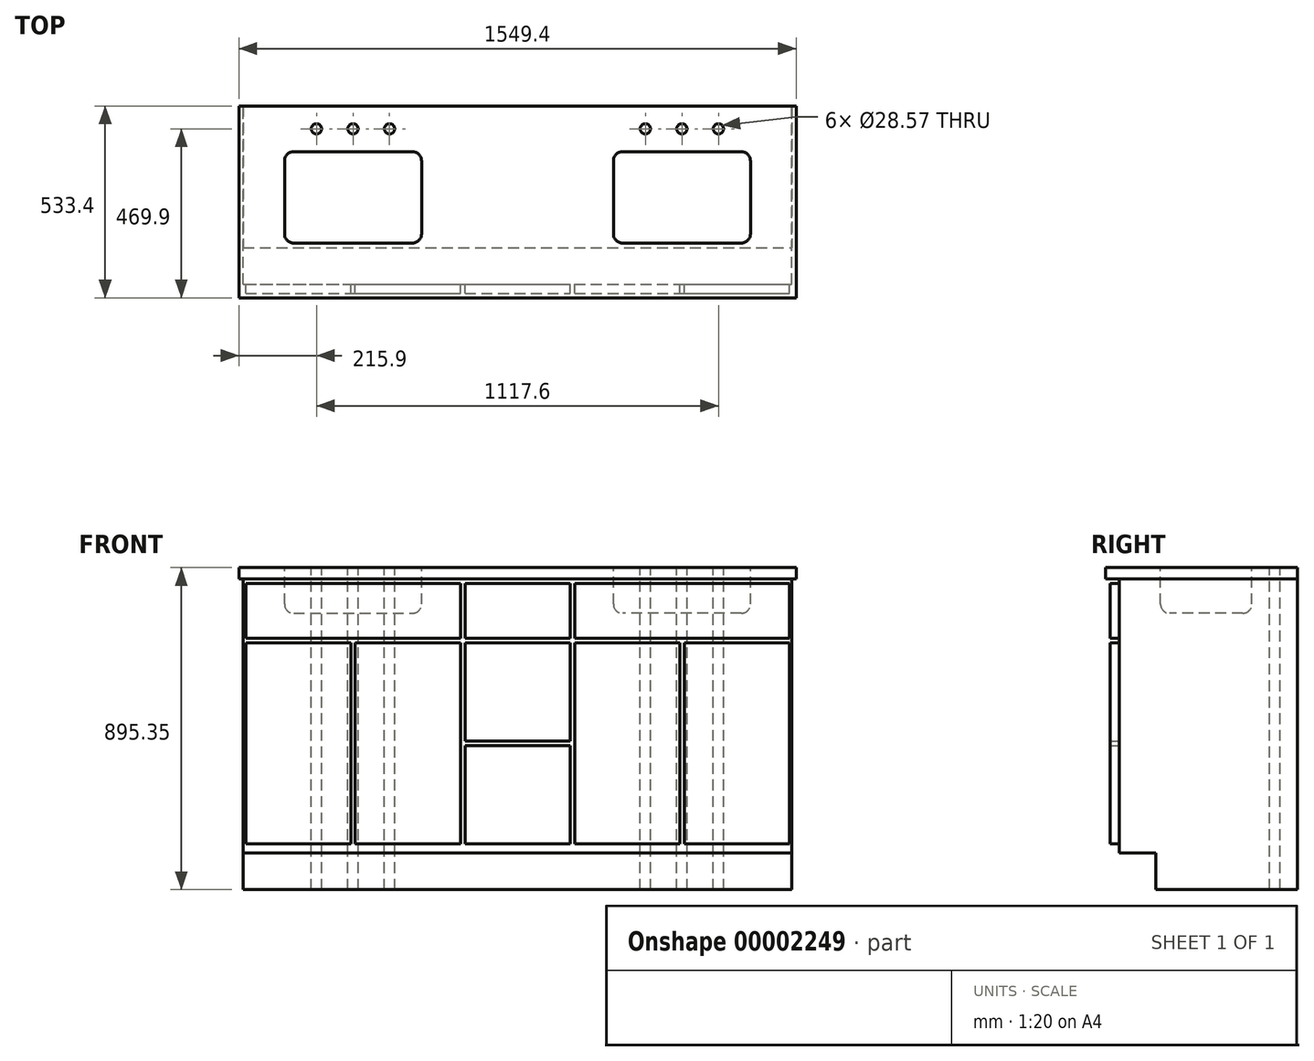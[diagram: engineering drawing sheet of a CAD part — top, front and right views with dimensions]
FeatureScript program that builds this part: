
annotation { "Feature Type Name" : "Feature", "Feature Type Description" : "" }
export const myFeature = defineFeature(function(context is Context, id is Id, definition is map)
    precondition{}
    {
        {
            var Q0;
            Q0=qCreatedBy(makeId("Right.planeOp"),FACE);
            var sketch = newSketch(context, id + "F0", { "sketchPlane" : qUnion([Q0])});
            skLineSegment(sketch, "E0.bottom", {"start": v(0, 0) * mm, "end": v(-393.7, 0) * mm});
            skLineSegment(sketch, "E0.left", {"start": v(0, 0) * mm, "end": v(0, 895.35) * mm});
            skLineSegment(sketch, "E0.right", {"start": v(-495.3, 101.6) * mm, "end": v(-495.3, 863.6) * mm});
            skLineSegment(sketch, "E1.top", {"start": v(-495.3, 101.6) * mm, "end": v(-393.7, 101.6) * mm});
            skLineSegment(sketch, "E1.right", {"start": v(-393.7, 0) * mm, "end": v(-393.7, 101.6) * mm});
            skLineSegment(sketch, "E2.bottom", {"start": v(-495.3, 863.6) * mm, "end": v(-533.4, 863.6) * mm});
            skLineSegment(sketch, "E2.top", {"start": v(0, 895.35) * mm, "end": v(-533.4, 895.35) * mm});
            skLineSegment(sketch, "E2.right", {"start": v(-533.4, 863.6) * mm, "end": v(-533.4, 895.35) * mm});
            skSolve(sketch);
        }
        {
            var Q0;
            Q0=makeQuery(id+"F0.imprint","IMPRINT",FACE,{"disambiguationData":[TD([[makeQuery(id+"F0.imprint","IMPRINT",EDGE,{"derivedFrom":sQuery(id+"F0.wireOp",EDGE,"E0.bottom")}),-1.0]])]});
            extrude(context, id + "F1", {"entities" : qUnion([Q0]), "oppositeDirection" : true, "depth" : 1524 * mm});
        }
        {
            var Q0;
            Q0=makeQuery(id+"F1.opExtrude","SWEPT_FACE",FACE,{"disambiguationData":[OSD([sQuery(id+"F0.wireOp",EDGE,"E0.right")])]});
            var sketch = newSketch(context, id + "F2", { "sketchPlane" : qUnion([Q0])});
            skLineSegment(sketch, "E3.bottom", {"start": v(-1517.65, 850.9) * mm, "end": v(-920.75, 850.9) * mm});
            skLineSegment(sketch, "E3.top", {"start": v(-1517.65, 698.5) * mm, "end": v(-920.75, 698.5) * mm});
            skLineSegment(sketch, "E3.left", {"start": v(-1517.65, 850.9) * mm, "end": v(-1517.65, 698.5) * mm});
            skLineSegment(sketch, "E3.right", {"start": v(-920.75, 850.9) * mm, "end": v(-920.75, 698.5) * mm});
            skLineSegment(sketch, "E4.bottom", {"start": v(-908.05, 850.9) * mm, "end": v(-615.95, 850.9) * mm});
            skLineSegment(sketch, "E4.top", {"start": v(-908.05, 698.5) * mm, "end": v(-615.95, 698.5) * mm});
            skLineSegment(sketch, "E4.left", {"start": v(-908.05, 850.9) * mm, "end": v(-908.05, 698.5) * mm});
            skLineSegment(sketch, "E4.right", {"start": v(-615.95, 850.9) * mm, "end": v(-615.95, 698.5) * mm});
            skLineSegment(sketch, "E5.bottom", {"start": v(-603.25, 850.9) * mm, "end": v(-6.35, 850.9) * mm});
            skLineSegment(sketch, "E5.top", {"start": v(-603.25, 698.5) * mm, "end": v(-6.35, 698.5) * mm});
            skLineSegment(sketch, "E5.left", {"start": v(-603.25, 850.9) * mm, "end": v(-603.25, 698.5) * mm});
            skLineSegment(sketch, "E5.right", {"start": v(-6.35, 850.9) * mm, "end": v(-6.35, 698.5) * mm});
            skLineSegment(sketch, "E6.bottom", {"start": v(-908.05, 685.8) * mm, "end": v(-615.95, 685.8) * mm});
            skLineSegment(sketch, "E6.top", {"start": v(-908.05, 412.75) * mm, "end": v(-615.95, 412.75) * mm});
            skLineSegment(sketch, "E6.left", {"start": v(-908.05, 685.8) * mm, "end": v(-908.05, 412.75) * mm});
            skLineSegment(sketch, "E6.right", {"start": v(-615.95, 685.8) * mm, "end": v(-615.95, 412.75) * mm});
            skLineSegment(sketch, "E7.bottom", {"start": v(-908.05, 400.05) * mm, "end": v(-615.95, 400.05) * mm});
            skLineSegment(sketch, "E7.top", {"start": v(-908.05, 127) * mm, "end": v(-615.95, 127) * mm});
            skLineSegment(sketch, "E7.left", {"start": v(-908.05, 400.05) * mm, "end": v(-908.05, 127) * mm});
            skLineSegment(sketch, "E7.right", {"start": v(-615.95, 400.05) * mm, "end": v(-615.95, 127) * mm});
            skLineSegment(sketch, "E8.bottom", {"start": v(-1517.65, 685.8) * mm, "end": v(-1225.55, 685.8) * mm});
            skLineSegment(sketch, "E8.top", {"start": v(-1517.65, 127) * mm, "end": v(-1225.55, 127) * mm});
            skLineSegment(sketch, "E8.left", {"start": v(-1517.65, 685.8) * mm, "end": v(-1517.65, 127) * mm});
            skLineSegment(sketch, "E8.right", {"start": v(-1225.55, 685.8) * mm, "end": v(-1225.55, 127) * mm});
            skLineSegment(sketch, "E9.bottom", {"start": v(-1212.85, 685.8) * mm, "end": v(-920.75, 685.8) * mm});
            skLineSegment(sketch, "E9.top", {"start": v(-1212.85, 127) * mm, "end": v(-920.75, 127) * mm});
            skLineSegment(sketch, "E9.left", {"start": v(-1212.85, 685.8) * mm, "end": v(-1212.85, 127) * mm});
            skLineSegment(sketch, "E9.right", {"start": v(-920.75, 685.8) * mm, "end": v(-920.75, 127) * mm});
            skLineSegment(sketch, "E10.bottom", {"start": v(-603.25, 685.8) * mm, "end": v(-311.15, 685.8) * mm});
            skLineSegment(sketch, "E10.top", {"start": v(-603.25, 127) * mm, "end": v(-311.15, 127) * mm});
            skLineSegment(sketch, "E10.left", {"start": v(-603.25, 685.8) * mm, "end": v(-603.25, 127) * mm});
            skLineSegment(sketch, "E10.right", {"start": v(-311.15, 685.8) * mm, "end": v(-311.15, 127) * mm});
            skLineSegment(sketch, "E11.bottom", {"start": v(-298.45, 685.8) * mm, "end": v(-6.35, 685.8) * mm});
            skLineSegment(sketch, "E11.top", {"start": v(-298.45, 127) * mm, "end": v(-6.35, 127) * mm});
            skLineSegment(sketch, "E11.left", {"start": v(-298.45, 685.8) * mm, "end": v(-298.45, 127) * mm});
            skLineSegment(sketch, "E11.right", {"start": v(-6.35, 685.8) * mm, "end": v(-6.35, 127) * mm});
            skSolve(sketch);
        }
        {
            var Q0;
            Q0=makeQuery(id+"F2.imprint","IMPRINT",FACE,{"disambiguationData":[TD([[makeQuery(id+"F2.imprint","IMPRINT",EDGE,{"derivedFrom":sQuery(id+"F2.wireOp",EDGE,"e1ef9630-6fec-4d97-9ac0-c20cbc9bf529.3")}),-1.0]])]});
            var Q1;
            Q1=makeQuery(id+"F2.imprint","IMPRINT",FACE,{"disambiguationData":[TD([[makeQuery(id+"F2.imprint","IMPRINT",EDGE,{"derivedFrom":sQuery(id+"F2.wireOp",EDGE,"b5957af1-2dda-447e-bfd9-5532a77e66a5.0")}),-1.0]])]});
            var Q2;
            Q2=makeQuery(id+"F2.imprint","IMPRINT",FACE,{"disambiguationData":[TD([[makeQuery(id+"F2.imprint","IMPRINT",EDGE,{"derivedFrom":sQuery(id+"F2.wireOp",EDGE,"d213ee8b-bd27-44e1-98d4-293f2c210446")}),1.0]])]});
            var Q3;
            Q3=makeQuery(id+"F2.imprint","IMPRINT",FACE,{"disambiguationData":[TD([[makeQuery(id+"F2.imprint","IMPRINT",EDGE,{"derivedFrom":sQuery(id+"F2.wireOp",EDGE,"fa58446a-992c-45ee-9411-d47b13bb5c77")}),1.0]])]});
            var Q4;
            {var subQ2=sQuery(id+"F2.wireOp",EDGE,"83c15fec-cbe0-4c30-b4af-53907da3e88f.0");Q4=makeQuery(id+"F2.imprint","IMPRINT",FACE,{"disambiguationData":[TD([[makeQuery(id+"F2.imprint","IMPRINT",EDGE,{"derivedFrom":subQ2}),1.0]])]});}
            var Q5;
            Q5=makeQuery(id+"F2.imprint","IMPRINT",FACE,{"disambiguationData":[TD([[makeQuery(id+"F2.imprint","IMPRINT",EDGE,{"derivedFrom":sQuery(id+"F2.wireOp",EDGE,"ccee0c31-25a3-4e00-ad5d-8d59a89c3470")}),-1.0]])]});
            var Q6;
            {var subQ2=sQuery(id+"F2.wireOp",EDGE,"e1ef9630-6fec-4d97-9ac0-c20cbc9bf529.0");Q6=makeQuery(id+"F2.imprint","IMPRINT",FACE,{"disambiguationData":[TD([[makeQuery(id+"F2.imprint","IMPRINT",EDGE,{"derivedFrom":subQ2}),1.0]])]});}
            var Q7;
            Q7=makeQuery(id+"F2.imprint","IMPRINT",FACE,{"disambiguationData":[TD([[makeQuery(id+"F2.imprint","IMPRINT",EDGE,{"derivedFrom":sQuery(id+"F2.wireOp",EDGE,"e1ef9630-6fec-4d97-9ac0-c20cbc9bf529.1")}),1.0]])]});
            var Q8;
            Q8=makeQuery(id+"F2.imprint","IMPRINT",FACE,{"disambiguationData":[TD([[makeQuery(id+"F2.imprint","IMPRINT",EDGE,{"derivedFrom":sQuery(id+"F2.wireOp",EDGE,"94968935-6469-4bd7-b6ec-2cd1eeb32554")}),1.0]])]});
            var Q9;
            Q9=makeQuery(id+"F2.imprint","IMPRINT",FACE,{"disambiguationData":[TD([[makeQuery(id+"F2.imprint","IMPRINT",EDGE,{"derivedFrom":sQuery(id+"F2.wireOp",EDGE,"E3.bottom")}),-1.0]])]});
            var Q10;
            Q10=makeQuery(id+"F2.imprint","IMPRINT",FACE,{"disambiguationData":[TD([[makeQuery(id+"F2.imprint","IMPRINT",EDGE,{"derivedFrom":sQuery(id+"F2.wireOp",EDGE,"E8.bottom")}),-1.0]])]});
            var Q11;
            Q11=makeQuery(id+"F2.imprint","IMPRINT",FACE,{"disambiguationData":[TD([[makeQuery(id+"F2.imprint","IMPRINT",EDGE,{"derivedFrom":sQuery(id+"F2.wireOp",EDGE,"E9.bottom")}),-1.0]])]});
            var Q12;
            Q12=makeQuery(id+"F2.imprint","IMPRINT",FACE,{"disambiguationData":[TD([[makeQuery(id+"F2.imprint","IMPRINT",EDGE,{"derivedFrom":sQuery(id+"F2.wireOp",EDGE,"E6.bottom")}),-1.0]])]});
            var Q13;
            Q13=makeQuery(id+"F2.imprint","IMPRINT",FACE,{"disambiguationData":[TD([[makeQuery(id+"F2.imprint","IMPRINT",EDGE,{"derivedFrom":sQuery(id+"F2.wireOp",EDGE,"E4.bottom")}),-1.0]])]});
            var Q14;
            Q14=makeQuery(id+"F2.imprint","IMPRINT",FACE,{"disambiguationData":[TD([[makeQuery(id+"F2.imprint","IMPRINT",EDGE,{"derivedFrom":sQuery(id+"F2.wireOp",EDGE,"E5.bottom")}),-1.0]])]});
            var Q15;
            Q15=makeQuery(id+"F2.imprint","IMPRINT",FACE,{"disambiguationData":[TD([[makeQuery(id+"F2.imprint","IMPRINT",EDGE,{"derivedFrom":sQuery(id+"F2.wireOp",EDGE,"E10.bottom")}),-1.0]])]});
            var Q16;
            Q16=makeQuery(id+"F2.imprint","IMPRINT",FACE,{"disambiguationData":[TD([[makeQuery(id+"F2.imprint","IMPRINT",EDGE,{"derivedFrom":sQuery(id+"F2.wireOp",EDGE,"E11.bottom")}),-1.0]])]});
            var Q17;
            Q17=makeQuery(id+"F2.imprint","IMPRINT",FACE,{"disambiguationData":[TD([[makeQuery(id+"F2.imprint","IMPRINT",EDGE,{"derivedFrom":sQuery(id+"F2.wireOp",EDGE,"E7.bottom")}),-1.0]])]});
            extrude(context, id + "F3", {"entities" : qUnion([Q0, Q1, Q2, Q3, Q4, Q5, Q6, Q7, Q8, Q9, Q10, Q11, Q12, Q13, Q14, Q15, Q16, Q17]), "operationType" : NewBodyOperationType.ADD, "depth" : 25.4 * mm});
        }
        {
            var Q0;
            Q0=makeQuery(id+"F1.opExtrude","CAP_FACE",FACE,{"disambiguationData":[OSD([sQuery(id+"F0.wireOp",EDGE,"E0.bottom"),sQuery(id+"F0.wireOp",EDGE,"E0.left"),sQuery(id+"F0.wireOp",EDGE,"E0.right"),sQuery(id+"F0.wireOp",EDGE,"E1.top"),sQuery(id+"F0.wireOp",EDGE,"E1.right"),sQuery(id+"F0.wireOp",EDGE,"E2.bottom"),sQuery(id+"F0.wireOp",EDGE,"E2.top"),sQuery(id+"F0.wireOp",EDGE,"E2.right")])],"isStart":false});
            var sketch = newSketch(context, id + "F4", { "sketchPlane" : qUnion([Q0])});
            skLineSegment(sketch, "E12.bottom", {"start": v(533.4, 863.6) * mm, "end": v(0, 863.6) * mm});
            skLineSegment(sketch, "E12.top", {"start": v(533.4, 895.35) * mm, "end": v(0, 895.35) * mm});
            skLineSegment(sketch, "E12.left", {"start": v(533.4, 863.6) * mm, "end": v(533.4, 895.35) * mm});
            skLineSegment(sketch, "E12.right", {"start": v(0, 863.6) * mm, "end": v(0, 895.35) * mm});
            skSolve(sketch);
        }
        {
            var Q0;
            Q0=makeQuery(id+"F4.imprint","IMPRINT",FACE,{"disambiguationData":[TD([[makeQuery(id+"F4.imprint","IMPRINT",EDGE,{"derivedFrom":sQuery(id+"F4.wireOp",EDGE,"E12.top")}),-1.0]])]});
            extrude(context, id + "F5", {"entities" : qUnion([Q0]), "operationType" : NewBodyOperationType.ADD, "depth" : 12.7 * mm, "hasSecondDirection" : true, "secondDirectionOppositeDirection" : true, "secondDirectionDepth" : 1536.7 * mm});
        }
        {
            var Q0;
            Q0=makeQuery(id+"F1.opExtrude","SWEPT_FACE",FACE,{"disambiguationData":[OSD([sQuery(id+"F0.wireOp",EDGE,"E2.top")])]});
            var sketch = newSketch(context, id + "F6", { "sketchPlane" : qUnion([Q0])});
            skLineSegment(sketch, "E13.bottom", {"start": v(-1409.7, -127) * mm, "end": v(-1028.7, -127) * mm});
            skLineSegment(sketch, "E13.top", {"start": v(-1409.7, -381) * mm, "end": v(-1028.7, -381) * mm});
            skLineSegment(sketch, "E13.left", {"start": v(-1409.7, -127) * mm, "end": v(-1409.7, -381) * mm});
            skLineSegment(sketch, "E13.right", {"start": v(-1028.7, -127) * mm, "end": v(-1028.7, -381) * mm});
            skLineSegment(sketch, "E14", {"start": v(-1219.2, -127) * mm, "end": v(-1219.2, -381) * mm, "construction": true});
            skLineSegment(sketch, "E15", {"start": v(-1219.2, 0) * mm, "end": v(-1219.2, -127) * mm});
            skLineSegment(sketch, "E16", {"start": v(-762, 0) * mm, "end": v(-762, -183.16) * mm, "construction": true});
            skLineSegment(sketch, "E17.0.MirrorCS", {"start": v(-114.3, -127) * mm, "end": v(-495.3, -127) * mm});
            skLineSegment(sketch, "E17.1.MirrorCS", {"start": v(-304.8, 0) * mm, "end": v(-304.8, -127) * mm});
            skLineSegment(sketch, "E17.2.MirrorCS", {"start": v(-114.3, -381) * mm, "end": v(-495.3, -381) * mm});
            skLineSegment(sketch, "E17.3.MirrorCS", {"start": v(-304.8, -127) * mm, "end": v(-304.8, -381) * mm, "construction": true});
            skLineSegment(sketch, "E17.4.MirrorCS", {"start": v(-495.3, -127) * mm, "end": v(-495.3, -381) * mm});
            skLineSegment(sketch, "E17.5.MirrorCS", {"start": v(-114.3, -127) * mm, "end": v(-114.3, -381) * mm});
            skSolve(sketch);
        }
        {
            var Q0;
            {Q0=qUnion([makeQuery(id+"F6.imprint","IMPRINT",FACE,{"disambiguationData":[TD([[makeQuery(id+"F6.imprint","IMPRINT",EDGE,{"derivedFrom":sQuery(id+"F6.wireOp",EDGE,"E13.top")}),1.0]])]}),makeQuery(id+"F6.imprint","IMPRINT",FACE,{"disambiguationData":[TD([[makeQuery(id+"F6.imprint","IMPRINT",EDGE,{"derivedFrom":sQuery(id+"F6.wireOp",EDGE,"E17.2.MirrorCS")}),-1.0]])]})]);}
            extrude(context, id + "F7", {"entities" : qUnion([Q0]), "operationType" : NewBodyOperationType.REMOVE, "oppositeDirection" : true, "depth" : 127 * mm});
        }
        {
            var Q0;
            Q0=makeQuery(id+"F7.boolean.opBoolean","COPY",EDGE,{"derivedFrom":makeQuery(id+"F7.opExtrude","SWEPT_EDGE",EDGE,{"disambiguationData":[OSD([sQuery(id+"F6.wireOp",EDGE,"E13.bottom"),sQuery(id+"F6.wireOp",EDGE,"E13.left")])]})});
            var Q1;
            Q1=makeQuery(id+"F7.boolean.opBoolean","COPY",EDGE,{"derivedFrom":makeQuery(id+"F7.opExtrude","SWEPT_EDGE",EDGE,{"disambiguationData":[OSD([sQuery(id+"F6.wireOp",EDGE,"E13.bottom"),sQuery(id+"F6.wireOp",EDGE,"E13.right")])]})});
            var Q2;
            Q2=makeQuery(id+"F7.boolean.opBoolean","COPY",EDGE,{"derivedFrom":makeQuery(id+"F7.opExtrude","SWEPT_EDGE",EDGE,{"disambiguationData":[OSD([sQuery(id+"F6.wireOp",EDGE,"E13.top"),sQuery(id+"F6.wireOp",EDGE,"E13.right")])]})});
            var Q3;
            Q3=makeQuery(id+"F7.boolean.opBoolean","COPY",EDGE,{"derivedFrom":makeQuery(id+"F7.opExtrude","SWEPT_EDGE",EDGE,{"disambiguationData":[OSD([sQuery(id+"F6.wireOp",EDGE,"E13.top"),sQuery(id+"F6.wireOp",EDGE,"E13.left")])]})});
            var Q4;
            Q4=makeQuery(id+"F7.boolean.opBoolean","COPY",EDGE,{"derivedFrom":makeQuery(id+"F7.opExtrude","SWEPT_EDGE",EDGE,{"disambiguationData":[OSD([sQuery(id+"F6.wireOp",EDGE,"E17.0.MirrorCS"),sQuery(id+"F6.wireOp",EDGE,"E17.4.MirrorCS")])]})});
            var Q5;
            Q5=makeQuery(id+"F7.boolean.opBoolean","COPY",EDGE,{"derivedFrom":makeQuery(id+"F7.opExtrude","SWEPT_EDGE",EDGE,{"disambiguationData":[OSD([sQuery(id+"F6.wireOp",EDGE,"E17.2.MirrorCS"),sQuery(id+"F6.wireOp",EDGE,"E17.5.MirrorCS")])]})});
            var Q6;
            Q6=makeQuery(id+"F7.boolean.opBoolean","COPY",EDGE,{"derivedFrom":makeQuery(id+"F7.opExtrude","SWEPT_EDGE",EDGE,{"disambiguationData":[OSD([sQuery(id+"F6.wireOp",EDGE,"E17.0.MirrorCS"),sQuery(id+"F6.wireOp",EDGE,"E17.5.MirrorCS")])]})});
            var Q7;
            Q7=makeQuery(id+"F7.boolean.opBoolean","COPY",EDGE,{"derivedFrom":makeQuery(id+"F7.opExtrude","SWEPT_EDGE",EDGE,{"disambiguationData":[OSD([sQuery(id+"F6.wireOp",EDGE,"E17.2.MirrorCS"),sQuery(id+"F6.wireOp",EDGE,"E17.4.MirrorCS")])]})});
            fillet(context, id + "F8", {"entities" : qUnion([Q0, Q1, Q2, Q3, Q4, Q5, Q6, Q7]), "radius" : 25.4 * mm, "tangentPropagation" : true, "allowEdgeOverflow" : false});
        }
        {
            var Q0;
            Q0=makeQuery(id+"F7.boolean.opBoolean","COPY",EDGE,{"derivedFrom":makeQuery(id+"F7.opExtrude","CAP_EDGE",EDGE,{"disambiguationData":[OSD([sQuery(id+"F6.wireOp",EDGE,"E13.bottom")])],"isStart":false})});
            var Q1;
            Q1=makeQuery(id+"F7.boolean.opBoolean","COPY",EDGE,{"derivedFrom":makeQuery(id+"F7.opExtrude","CAP_EDGE",EDGE,{"disambiguationData":[OSD([sQuery(id+"F6.wireOp",EDGE,"E17.2.MirrorCS")])],"isStart":false})});
            fillet(context, id + "F9", {"entities" : qUnion([Q0, Q1]), "radius" : 25.4 * mm, "tangentPropagation" : true, "allowEdgeOverflow" : false});
        }
        {
            var Q0;
            Q0=makeQuery(id+"F1.opExtrude","SWEPT_FACE",FACE,{"disambiguationData":[OSD([sQuery(id+"F0.wireOp",EDGE,"E2.top")])]});
            var sketch = newSketch(context, id + "F10", { "sketchPlane" : qUnion([Q0])});
            skCircle(sketch, "E18", {"center": v(-1219.2, -63.5) * mm, "radius": 14.29 * mm});
            skLineSegment(sketch, "E19", {"start": v(-1219.2, -127) * mm, "end": v(-1219.2, -63.5) * mm, "construction": true});
            skLineSegment(sketch, "E20", {"start": v(-304.8, -127) * mm, "end": v(-304.8, -63.5) * mm, "construction": true});
            skLineSegment(sketch, "E21", {"start": v(-1320.8, -63.5) * mm, "end": v(-1117.6, -63.5) * mm, "construction": true});
            skLineSegment(sketch, "E22", {"start": v(-406.4, -63.5) * mm, "end": v(-203.2, -63.5) * mm, "construction": true});
            skCircle(sketch, "E23", {"center": v(-1320.8, -63.5) * mm, "radius": 14.29 * mm});
            skCircle(sketch, "E24", {"center": v(-1117.6, -63.5) * mm, "radius": 14.29 * mm});
            skCircle(sketch, "E25", {"center": v(-406.4, -63.5) * mm, "radius": 14.29 * mm});
            skCircle(sketch, "E26", {"center": v(-304.8, -63.5) * mm, "radius": 14.29 * mm});
            skCircle(sketch, "E27", {"center": v(-203.2, -63.5) * mm, "radius": 14.29 * mm});
            skSolve(sketch);
        }
        {
            var Q0;
            Q0 = qSketchRegion(id + "F10", true);
            extrude(context, id + "F11", {"entities" : qUnion([Q0]), "operationType" : NewBodyOperationType.REMOVE, "oppositeDirection" : true, "depth" : 914.4 * mm});
        }
    });
